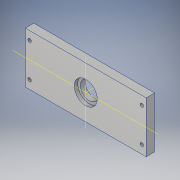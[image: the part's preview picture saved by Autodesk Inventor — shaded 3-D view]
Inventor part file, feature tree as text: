
AUTODESK INVENTOR PART (.ipt)
format: ipt  version: 2018 (Build 220112000, 112)  size: 127,488 bytes
history: native  units: mm
features: extrude x4, sketch x4, other x1
ambient origin geometry x8: Origin, YZ Plane, XZ Plane, XY Plane, X Axis, Y Axis, Z Axis, Center Point
bodies: Body1 (feature_tree)
feature tree (9):
  other  "ソリッド1"
  extrude  "押し出し1"  Depth=60.0mm
  extrude  "押し出し2"  Depth=142.0mm
  extrude  "押し出し3"  Depth=10.0mm TaperAngle=0.0deg
  extrude  "押し出し4"  Depth=27.0mm
  sketch  "スケッチ3"
  sketch  "スケッチ4"
  sketch  "スケッチ5"
  sketch  "スケッチ6"
